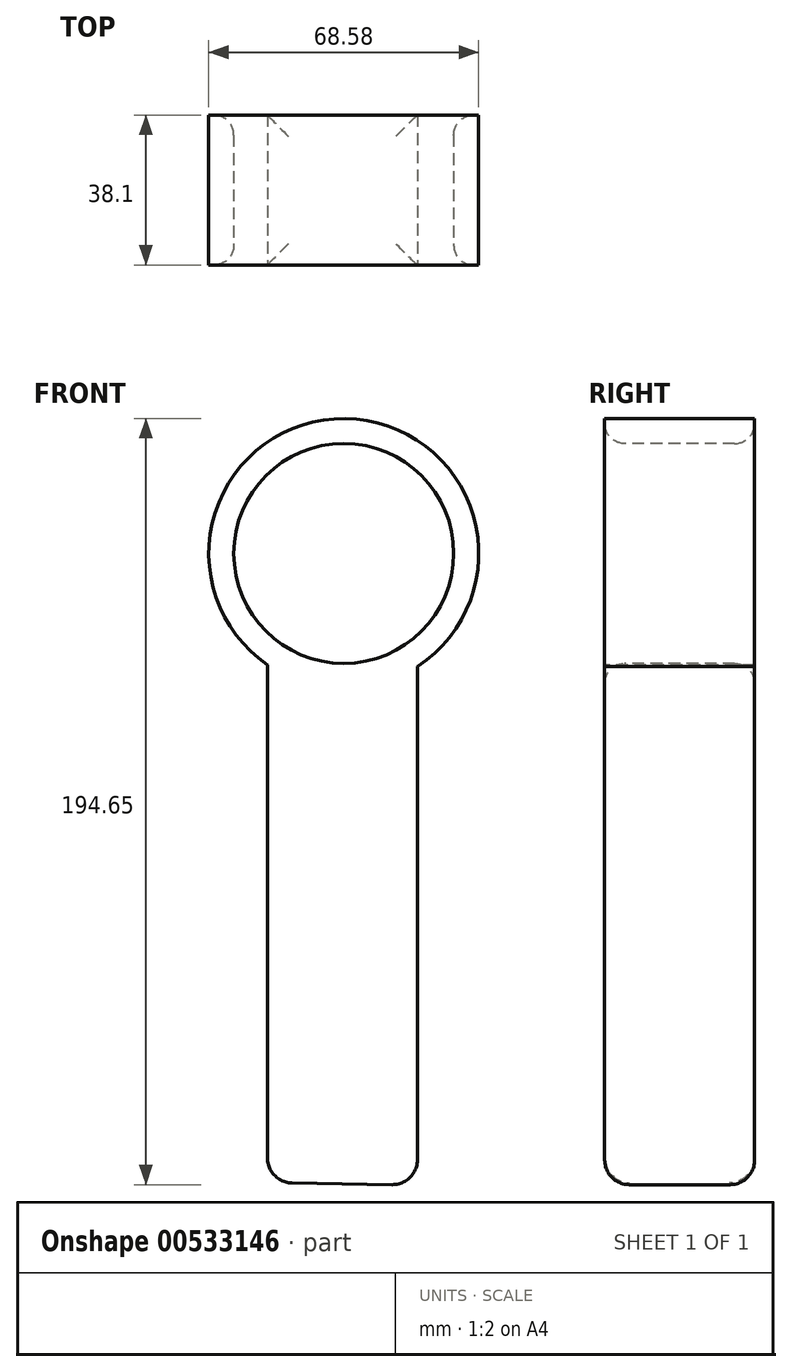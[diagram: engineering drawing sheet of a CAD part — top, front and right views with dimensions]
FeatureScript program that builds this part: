
annotation { "Feature Type Name" : "Feature", "Feature Type Description" : "" }
export const myFeature = defineFeature(function(context is Context, id is Id, definition is map)
    precondition{}
    {
        {
            var Q0;
            Q0=qCreatedBy(makeId("Front.planeOp"),FACE);
            var sketch = newSketch(context, id + "F0", { "sketchPlane" : qUnion([Q0])});
            skCircle(sketch, "E0", {"center": v(0, 0) * mm, "radius": 34.3 * mm});
            skCircle(sketch, "E1", {"center": v(0, 0) * mm, "radius": 27.94 * mm});
            skSolve(sketch);
        }
        {
            var Q0;
            Q0=makeQuery(id+"F0.imprint","IMPRINT",FACE,{"disambiguationData":[TD([[makeQuery(id+"F0.imprint","IMPRINT",EDGE,{"derivedFrom":sQuery(id+"F0.wireOp",EDGE,"E0")}),1.0]])]});
            extrude(context, id + "F1", {"entities" : qUnion([Q0]), "oppositeDirection" : true, "depth" : 38.1 * mm, "offsetDistance" : 25.4 * mm});
        }
        {
            var Q0;
            Q0=makeQuery(id+"F1.opExtrude","CAP_FACE",FACE,{"disambiguationData":[OSD([sQuery(id+"F0.wireOp",EDGE,"E0"),sQuery(id+"F0.wireOp",EDGE,"E1")])],"isStart":true});
            var sketch = newSketch(context, id + "F2", { "sketchPlane" : qUnion([Q0])});
            skArc(sketch, "E2", {"start": v(-19.38, -20.16) * mm, "mid": v(-0.45, -27.95) * mm, "end": v(18.72, -20.76) * mm});
            skLineSegment(sketch, "E3", {"start": v(-19.38, -20.13) * mm, "end": v(-19.38, -159.83) * mm});
            skLineSegment(sketch, "E4", {"start": v(18.72, -20.76) * mm, "end": v(18.72, -160.46) * mm});
            skLineSegment(sketch, "E5", {"start": v(-19.38, -159.83) * mm, "end": v(18.72, -160.46) * mm});
            skSolve(sketch);
        }
        {
            var Q0;
            {var subQ0=sQuery(id+"F2.wireOp",EDGE,"E5");Q0=makeQuery(id+"F2.imprint","IMPRINT",FACE,{"disambiguationData":[TD([[makeQuery(id+"F2.imprint","IMPRINT",EDGE,{"derivedFrom":subQ0}),1.0]])]});}
            extrude(context, id + "F3", {"entities" : qUnion([Q0]), "operationType" : NewBodyOperationType.ADD, "oppositeDirection" : true, "depth" : 38.1 * mm, "offsetDistance" : 25.4 * mm});
        }
        {
            var Q0;
            Q0=makeQuery(id+"F3.opExtrude","CAP_EDGE",EDGE,{"disambiguationData":[OSD([sQuery(id+"F2.wireOp",EDGE,"E5")])],"isStart":true});
            var Q1;
            Q1=makeQuery(id+"F3.opExtrude","CAP_EDGE",EDGE,{"disambiguationData":[OSD([sQuery(id+"F2.wireOp",EDGE,"E5")])],"isStart":false});
            var Q2;
            Q2=makeQuery(id+"F3.opExtrude","SWEPT_EDGE",EDGE,{"disambiguationData":[OSD([sQuery(id+"F2.wireOp",EDGE,"E4"),sQuery(id+"F2.wireOp",EDGE,"E5")])]});
            var Q3;
            Q3=makeQuery(id+"F3.opExtrude","SWEPT_EDGE",EDGE,{"disambiguationData":[OSD([sQuery(id+"F2.wireOp",EDGE,"E3"),sQuery(id+"F2.wireOp",EDGE,"E5")])]});
            fillet(context, id + "F4", {"entities" : qUnion([Q0, Q1, Q2, Q3]), "radius" : 6.35 * mm, "tangentPropagation" : true, "allowEdgeOverflow" : false});
        }
        {
            var Q0;
            Q0=makeQuery(id+"F1.opExtrude","CAP_EDGE",EDGE,{"disambiguationData":[OSD([sQuery(id+"F0.wireOp",EDGE,"E1")])],"isStart":true});
            fillet(context, id + "F5", {"entities" : qUnion([Q0]), "radius" : 5.08 * mm, "tangentPropagation" : true, "allowEdgeOverflow" : false});
        }
        {
            var Q0;
            Q0=makeQuery(id+"F1.opExtrude","CAP_EDGE",EDGE,{"disambiguationData":[OSD([sQuery(id+"F0.wireOp",EDGE,"E1")])],"isStart":false});
            fillet(context, id + "F6", {"entities" : qUnion([Q0]), "radius" : 5.08 * mm, "tangentPropagation" : true, "allowEdgeOverflow" : false});
        }
    });
